# Revit family: IS_ConnectFreedom_E8244_BIM_DE
name_source: partatom
category: Plumbing Fixtures
revit_build: Autodesk Revit MEP 2016 (Build: 20161004_0715(x64)
units: mm (PartAtom-declared; Revit-internal decimal feet)

## family parameters
Always vertical = No
Cut with Voids When Loaded = No
OmniClass Number = 23.45.05.21.11.11
OmniClass Title = Water Operated Water Closets
Part Type = Normal
Room Calculation Point = No
Round Connector Dimension = Use Diameter
Shared = No
Work Plane-Based = No

## types (1)
- E824401 - CONNECT FREEDOM seat & cover with hinges
    Accessories = www.idealstandard.de\ersatzteile
    AssetType = Fixed
    BIMObjectName = ISI_IdealStandard_WcSeatsAndCovers_ConnectFreedom_E824401
    BIMobject category = Toilet Seats
    BOSUseNativeGeometries = 1
    BarCode = 5017830484028
    Brand = Ideal Standard
    Brand url = http://www.idealstandard.de
    Color = White
    ConnectionType = Plumbing
    Cost = 0 $
    CurrencyUnit = €
    CurrentRevision = 1
    Date of publishing = 20/12/2017
    Description = IS WC-Sitz CONNECT FREEDOM, mit Stangenscharnier, Weiß
    DurationUnit = Year
    EAN code = https://5017830484028
    Edition number = 1
    ExpectedLife = 25
    Features = IS WC-Sitz CONNECT FREEDOM, mit Stangenscharnier, Weiß
    Finish = White
    IFC Classification = Sanitary Terminal
    IfcExportAs = IfcSanitaryTerminalType
    Installation instructions = http://www.idealstandard.de
    InstallationInstructions = www.idealstandard.de\produkte
    MainColor = White
    MaintenanceInformation = www.idealstandard.de\produkte
    Manufacturer name = Ideal Standard
    ManufacturerURL = http://www.idealstandard.de
    Material = Duroplast
    Model = E824401
    ModelNumber = E824401
    ModelReference = IS WC-Sitz CONNECT FREEDOM, mit Stangenscharnier, Weiß
    NBS Reference Code = 35-93-95
    NBS Reference Description = Wc Seats And Covers
    Name = WcSeatsAndCovers_ConnectFreedom_E824401
    NettWeight = 2.1 Kg
    Nominal height = 45
    Nominal width = 365
    NominalDepth = 431 mm  [stored 1.41404 ft]
    NominalHeight = 40 mm
    NominalLength = 431 mm  [stored 1.41404 ft]
    NominalWidth = 365 mm  [stored 1.19751 ft]
    OmniClass Code = 23-31 19 00
    OmniClass Description = Toilets
    OutletConnectionSize = 0 mm  [stored 0 ft]
    Product Guid = 6db46996-9c27-49f7-9261-d348f14e9a0d
    Product SKU = E8244
    Product data url = https://bimobject.com
    Product family = Sanitary
    Product group = Seat & Cover
    Product name = CONNECT FREEDOM seat & cover with hinges
    Product url = http://www.idealstandard.de
    ProductInformation = www.idealstandard.de/produkte
    QR code = http://bimobject.com
    Shape = Sculptured
    Size = 40 x 431 x 465mm
    Space = Internal
    SpareParts = www.idealstandard.de/ersatzteile
    SpilloverLevel = 0 mm  [stored 0 ft]
    Technical description = http://www.idealstandard.de
    URL = http://www.idealstandard.de
    Uniclass 1.4 Code = L7216
    Uniclass 1.4 Description = Toilets
    Uniclass 2.0 Code = PR-35-93-95
    Uniclass 2.0 Description = Wc Seats And Covers
    Uniclass 2015 Code = Pr_40_20_93_95
    Uniclass 2015 Name = WC seats and covers
    Uniclass2015Code = Pr_40_20_93_95
    Uniclass2015Title = WC seats and covers
    Uniclass2015Version = Products v1.1
    Version = 1
    VolumeUnits = Litres
    Weight Net (Kg) = 2.1

note: [stored X ft] marks values corroborated as IEEE doubles in the binary element streams (Revit-internal decimal feet)

## geometry (parser evidence)
native form markers: Blend x4, Sweep x1
no freeform markers — native parametric forms only
